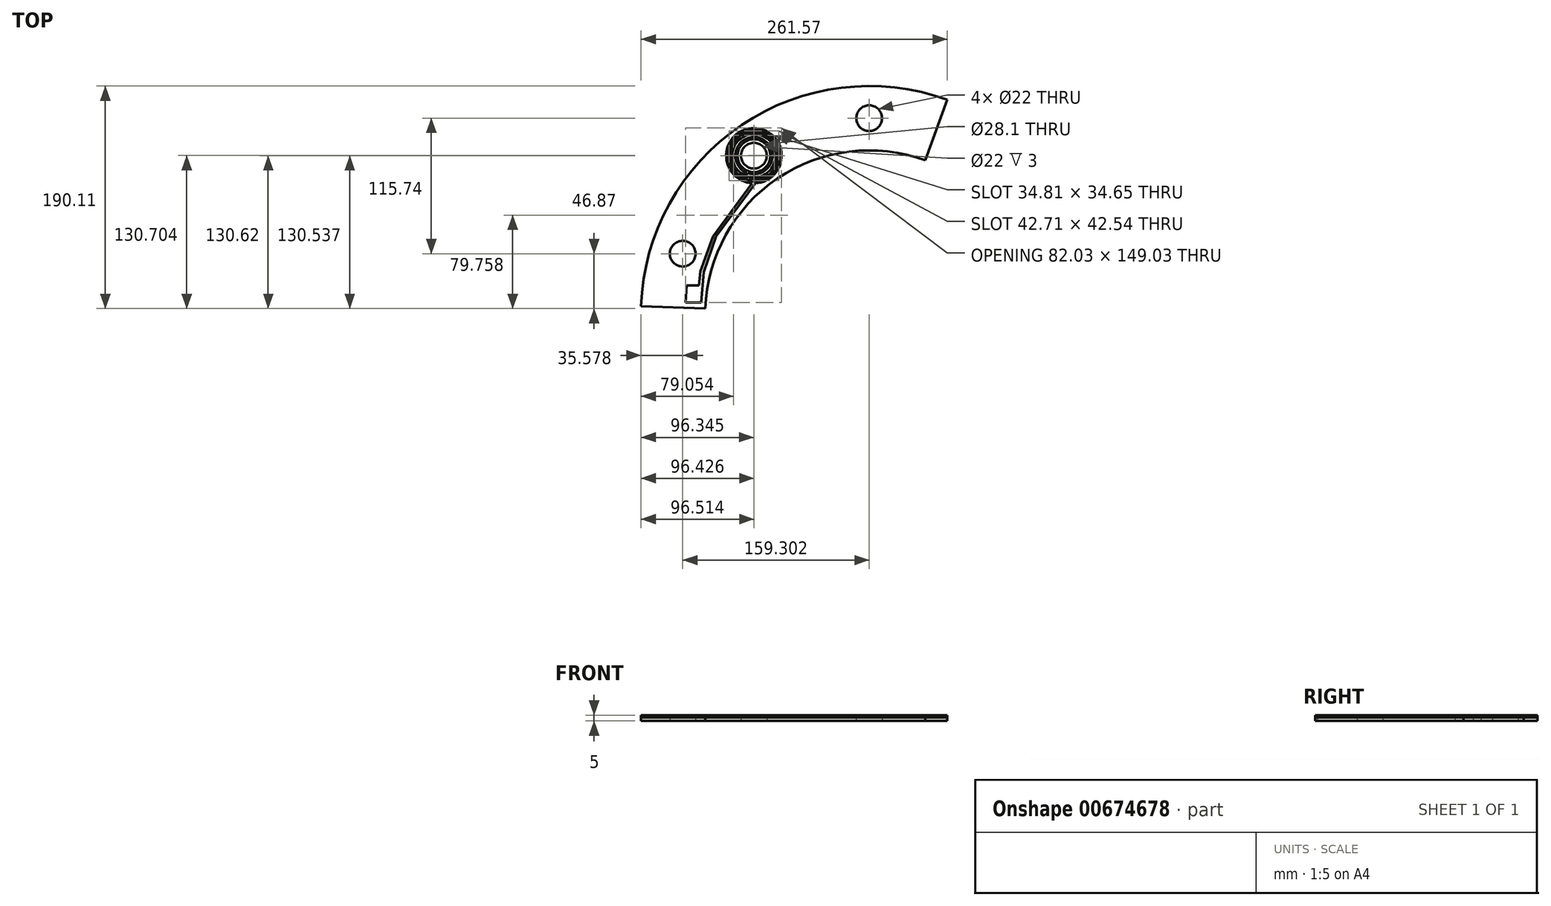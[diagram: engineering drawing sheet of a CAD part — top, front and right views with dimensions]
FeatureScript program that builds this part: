
annotation { "Feature Type Name" : "Feature", "Feature Type Description" : "" }
export const myFeature = defineFeature(function(context is Context, id is Id, definition is map)
    precondition{}
    {
        {
            var Q0;
            Q0=qCreatedBy(makeId("Top.planeOp"),FACE);
            var sketch = newSketch(context, id + "F0", { "sketchPlane" : qUnion([Q0])});
            skCircle(sketch, "E0", {"center": v(0, 0) * mm, "radius": 195 * mm});
            skLineSegment(sketch, "E1", {"start": v(-236.95, 0) * mm, "end": v(264.25, 0) * mm, "construction": true});
            skLineSegment(sketch, "E2", {"start": v(0, -228.62) * mm, "end": v(0, 236.65) * mm, "construction": true});
            skCircle(sketch, "E3", {"center": v(0, 0) * mm, "radius": 140 * mm});
            skCircle(sketch, "E4", {"center": v(0, 0) * mm, "radius": 167.5 * mm});
            skPoint(sketch, "E5", {"position": v(0, 167.5) * mm});
            skPoint(sketch, "E6.1.0", {"position": v(-98.45, 135.51) * mm});
            skPoint(sketch, "E6.2.0", {"position": v(-159.3, 51.76) * mm});
            skPoint(sketch, "E6.3.0", {"position": v(-159.3, -51.76) * mm});
            skPoint(sketch, "E6.4.0", {"position": v(-98.45, -135.51) * mm});
            skPoint(sketch, "E6.5.0", {"position": v(0, -167.5) * mm});
            skPoint(sketch, "E6.6.0", {"position": v(98.45, -135.51) * mm});
            skPoint(sketch, "E6.7.0", {"position": v(159.3, -51.76) * mm});
            skPoint(sketch, "E6.8.0", {"position": v(159.3, 51.76) * mm});
            skPoint(sketch, "E6.9.0", {"position": v(98.45, 135.51) * mm});
            skLineSegment(sketch, "E7", {"start": v(0, 0) * mm, "end": v(91.1, 250.3) * mm});
            skLineSegment(sketch, "E8", {"start": v(0, 0) * mm, "end": v(-87.39, -240.1) * mm});
            skLineSegment(sketch, "E9", {"start": v(0, 0) * mm, "end": v(-255.48, 8.92) * mm});
            skLineSegment(sketch, "E10", {"start": v(0, 0) * mm, "end": v(300.02, -10.48) * mm});
            skSolve(sketch);
        }
        {
            var Q0;
            {var subQ0=sQuery(id+"F0.wireOp",EDGE,"E9");var subQ1=sQuery(id+"F0.wireOp",EDGE,"E3");var subQ2=makeQuery(id+"F0.imprint","INTERSECT",VERTEX,{"derivedFrom":[subQ1,subQ0]});Q0=makeQuery(id+"F0.imprint","IMPRINT",FACE,{"disambiguationData":[TD([[makeQuery(id+"F0.imprint","IMPRINT",EDGE,{"disambiguationData":[TD([[subQ2,1.0]])],"derivedFrom":subQ1}),-1.0]])]});}
            var Q1;
            {var subQ0=sQuery(id+"F0.wireOp",EDGE,"E9");var subQ1=sQuery(id+"F0.wireOp",EDGE,"E0");var subQ2=makeQuery(id+"F0.imprint","INTERSECT",VERTEX,{"derivedFrom":[subQ1,subQ0]});Q1=makeQuery(id+"F0.imprint","IMPRINT",FACE,{"disambiguationData":[TD([[makeQuery(id+"F0.imprint","IMPRINT",EDGE,{"disambiguationData":[TD([[subQ2,1.0]])],"derivedFrom":subQ1}),1.0]])]});}
            extrude(context, id + "F1", {"entities" : qUnion([Q0, Q1]), "depth" : 3 * mm, "offsetDistance" : 25 * mm});
        }
        {
            var Q0;
            Q0=sQuery(id+"F0.wireOp",VERTEX,"E5");
            var Q1;
            Q1=sQuery(id+"F0.wireOp",VERTEX,"E6.1.0");
            var Q2;
            Q2=sQuery(id+"F0.wireOp",VERTEX,"E6.2.0");
            var Q3;
            Q3=makeQuery(id+"F1.opExtrude","SWEPT_BODY",BODY,{"disambiguationData":[OSD([sQuery(id+"F0.wireOp",EDGE,"E0"),sQuery(id+"F0.wireOp",EDGE,"E3"),sQuery(id+"F0.wireOp",EDGE,"E7"),sQuery(id+"F0.wireOp",EDGE,"7779584a-14d0-4c0c-a12f-be6d3e54e7f4.3.0")])]});
            hole(context, id + "F2", {"style" : HoleStyle.SIMPLE, "endStyle" : HoleEndStyle.THROUGH, "oppositeDirection" : true, "standardTappedOrClearance" : lookupTablePath({ "standard" : "ISO", "size" : "22", "type" : "Drilled" }), "standardBlindInLast" : lookupTablePath({ "standard" : "ISO", "size" : "22", "type" : "Drilled" }), "holeDiameter" : 22 * mm, "majorDiameter" : 5 * mm, "tappedDepth" : 30 * mm, "tapClearance" : 3, "locations" : qUnion([Q0, Q1, Q2]), "scope" : qUnion([Q3])});
        }
        {
            var Q0;
            Q0=makeQuery(id+"F1.opExtrude","CAP_FACE",FACE,{"disambiguationData":[OSD([sQuery(id+"F0.wireOp",EDGE,"E0"),sQuery(id+"F0.wireOp",EDGE,"E3"),sQuery(id+"F0.wireOp",EDGE,"E7"),sQuery(id+"F0.wireOp",EDGE,"E9")])],"isStart":false});
            var sketch = newSketch(context, id + "F3", { "sketchPlane" : qUnion([Q0])});
            skCircle(sketch, "E11", {"center": v(-98.45, 135.51) * mm, "radius": 14.05 * mm});
            skArc(sketch, "E12", {"start": v(-103.81, 120.52) * mm, "mid": v(-92.64, 150.33) * mm, "end": v(-104.73, 120.88) * mm});
            skArc(sketch, "E13", {"start": v(-105.8, 118.54) * mm, "mid": v(-90.67, 152.29) * mm, "end": v(-106.67, 118.94) * mm});
            skArc(sketch, "E14", {"start": v(-102.7, 115.4) * mm, "mid": v(-93.64, 155.48) * mm, "end": v(-103.83, 115.68) * mm});
            skArc(sketch, "E15", {"start": v(-103.8, 114.07) * mm, "mid": v(-92.48, 156.78) * mm, "end": v(-105.05, 114.42) * mm});
            skArc(sketch, "E16", {"start": v(-97.12, 111.9) * mm, "mid": v(-98.38, 159.16) * mm, "end": v(-99.93, 111.9) * mm});
            skLineSegment(sketch, "E17", {"start": v(-97.12, 111.9) * mm, "end": v(-130.67, 66.38) * mm});
            skLineSegment(sketch, "E18", {"start": v(-130.67, 66.38) * mm, "end": v(-141.4, 36.04) * mm});
            skLineSegment(sketch, "E19", {"start": v(-141.4, 36.04) * mm, "end": v(-143.42, 10.13) * mm});
            skLineSegment(sketch, "E20", {"start": v(-143.42, 10.13) * mm, "end": v(-156.84, 10.13) * mm});
            skLineSegment(sketch, "E21", {"start": v(-156.84, 10.13) * mm, "end": v(-155.77, 24.5) * mm});
            skLineSegment(sketch, "E22", {"start": v(-155.77, 24.5) * mm, "end": v(-145.43, 24.5) * mm});
            skLineSegment(sketch, "E23", {"start": v(-145.43, 24.5) * mm, "end": v(-144.1, 36.71) * mm});
            skLineSegment(sketch, "E24", {"start": v(-144.1, 36.71) * mm, "end": v(-133.49, 66.38) * mm});
            skLineSegment(sketch, "E25", {"start": v(-133.49, 66.38) * mm, "end": v(-99.93, 111.9) * mm});
            skLineSegment(sketch, "E26", {"start": v(-102.7, 115.4) * mm, "end": v(-103.8, 114.07) * mm});
            skLineSegment(sketch, "E27", {"start": v(-103.83, 115.68) * mm, "end": v(-105.05, 114.42) * mm});
            skLineSegment(sketch, "E28", {"start": v(-103.81, 120.52) * mm, "end": v(-105.8, 118.54) * mm});
            skLineSegment(sketch, "E29", {"start": v(-104.73, 120.88) * mm, "end": v(-106.67, 118.94) * mm});
            skSolve(sketch);
        }
        {
            var Q0;
            Q0=makeQuery(id+"F3.imprint","IMPRINT",FACE,{"disambiguationData":[TD([[makeQuery(id+"F3.imprint","IMPRINT",EDGE,{"derivedFrom":sQuery(id+"F3.wireOp",EDGE,"E11")}),-1.0]])]});
            extrude(context, id + "F4", {"entities" : qUnion([Q0]), "operationType" : NewBodyOperationType.REMOVE, "oppositeDirection" : true, "depth" : 0.5 * mm, "offsetDistance" : 25 * mm});
        }
        {
            var Q0;
            Q0=makeQuery(id+"F4.boolean.opBoolean","COPY",FACE,{"derivedFrom":makeQuery(id+"F4.opExtrude","CAP_FACE",FACE,{"disambiguationData":[OSD([sQuery(id+"F3.wireOp",EDGE,"E11"),sQuery(id+"F3.wireOp",EDGE,"E12"),sQuery(id+"F3.wireOp",EDGE,"E13"),sQuery(id+"F3.wireOp",EDGE,"E14"),sQuery(id+"F3.wireOp",EDGE,"E15"),sQuery(id+"F3.wireOp",EDGE,"E16"),sQuery(id+"F3.wireOp",EDGE,"E17"),sQuery(id+"F3.wireOp",EDGE,"E18"),sQuery(id+"F3.wireOp",EDGE,"E19"),sQuery(id+"F3.wireOp",EDGE,"E20"),sQuery(id+"F3.wireOp",EDGE,"E21"),sQuery(id+"F3.wireOp",EDGE,"E22"),sQuery(id+"F3.wireOp",EDGE,"E23"),sQuery(id+"F3.wireOp",EDGE,"E24"),sQuery(id+"F3.wireOp",EDGE,"E25"),sQuery(id+"F3.wireOp",EDGE,"E26"),sQuery(id+"F3.wireOp",EDGE,"E27"),sQuery(id+"F3.wireOp",EDGE,"E28"),sQuery(id+"F3.wireOp",EDGE,"E29")])],"isStart":false})});
            extrude(context, id + "F5", {"entities" : qUnion([Q0]), "depth" : 0.5 * mm, "offsetDistance" : 25 * mm});
        }
        {
            var Q0;
            {var subQ0=sQuery(id+"F0.wireOp",EDGE,"E0");var subQ1=sQuery(id+"F0.wireOp",EDGE,"E9");var subQ2=sQuery(id+"F0.wireOp",EDGE,"E3");var subQ3=sQuery(id+"F0.wireOp",EDGE,"E7");Q0=makeQuery(id+"F4.boolean.opBoolean","SPLIT",FACE,{"disambiguationData":[TD([makeQuery(id+"F1.opExtrude","SWEPT_FACE",FACE,{"disambiguationData":[OSD([subQ0])]})])],"derivedFrom":makeQuery(id+"F1.opExtrude","CAP_FACE",FACE,{"disambiguationData":[OSD([subQ0,subQ2,subQ3,subQ1])],"isStart":false})});}
            var sketch = newSketch(context, id + "F6", { "sketchPlane" : qUnion([Q0])});
            skSolve(sketch);
        }
        {
            var Q0;
            {var subQ3=sQuery(id+"F0.wireOp",EDGE,"E0");Q0=makeQuery(id+"F6.imprint","IMPRINT",FACE,{"disambiguationData":[TD([[makeQuery(id+"F6.imprint","IMPRINT",EDGE,{"derivedFrom":makeQuery(id+"F1.opExtrude","CAP_EDGE",EDGE,{"disambiguationData":[OSD([subQ3])],"isStart":false})}),1.0]])]});}
            var Q1;
            Q1=makeQuery(id+"F6.imprint","IMPRINT",FACE,{"disambiguationData":[TD([[makeQuery(id+"F6.imprint","IMPRINT",EDGE,{"derivedFrom":makeQuery(id+"F4.boolean.opBoolean","COPY",EDGE,{"derivedFrom":makeQuery(id+"F4.opExtrude","CAP_EDGE",EDGE,{"disambiguationData":[OSD([sQuery(id+"F3.wireOp",EDGE,"E16")])],"isStart":true})})}),1.0]])]});
            extrude(context, id + "F7", {"entities" : qUnion([Q0, Q1]), "depth" : 2 * mm, "offsetDistance" : 25 * mm});
        }
        {
            var Q0;
            Q0=sQuery(id+"F0.wireOp",VERTEX,"E6.1.0");
            var Q1;
            Q1=makeQuery(id+"F7.opExtrude","SWEPT_BODY",BODY,{"disambiguationData":[OSD([sQuery(id+"F0.wireOp",EDGE,"E0"),sQuery(id+"F0.wireOp",EDGE,"E3"),sQuery(id+"F0.wireOp",EDGE,"E7"),sQuery(id+"F0.wireOp",EDGE,"E9"),sQuery(id+"F2.hole-0.sketch.wireOp",EDGE,"core_line_2"),sQuery(id+"F2.hole-2.sketch.wireOp",EDGE,"core_line_2")])]});
            hole(context, id + "F8", {"style" : HoleStyle.SIMPLE, "endStyle" : HoleEndStyle.THROUGH, "oppositeDirection" : true, "standardTappedOrClearance" : lookupTablePath({ "standard" : "ISO", "size" : "22", "type" : "Drilled" }), "standardBlindInLast" : lookupTablePath({ "standard" : "ISO", "size" : "22", "type" : "Drilled" }), "holeDiameter" : 22 * mm, "majorDiameter" : 5 * mm, "tappedDepth" : 30 * mm, "tapClearance" : 3, "locations" : qUnion([Q0]), "scope" : qUnion([Q1])});
        }
    });
